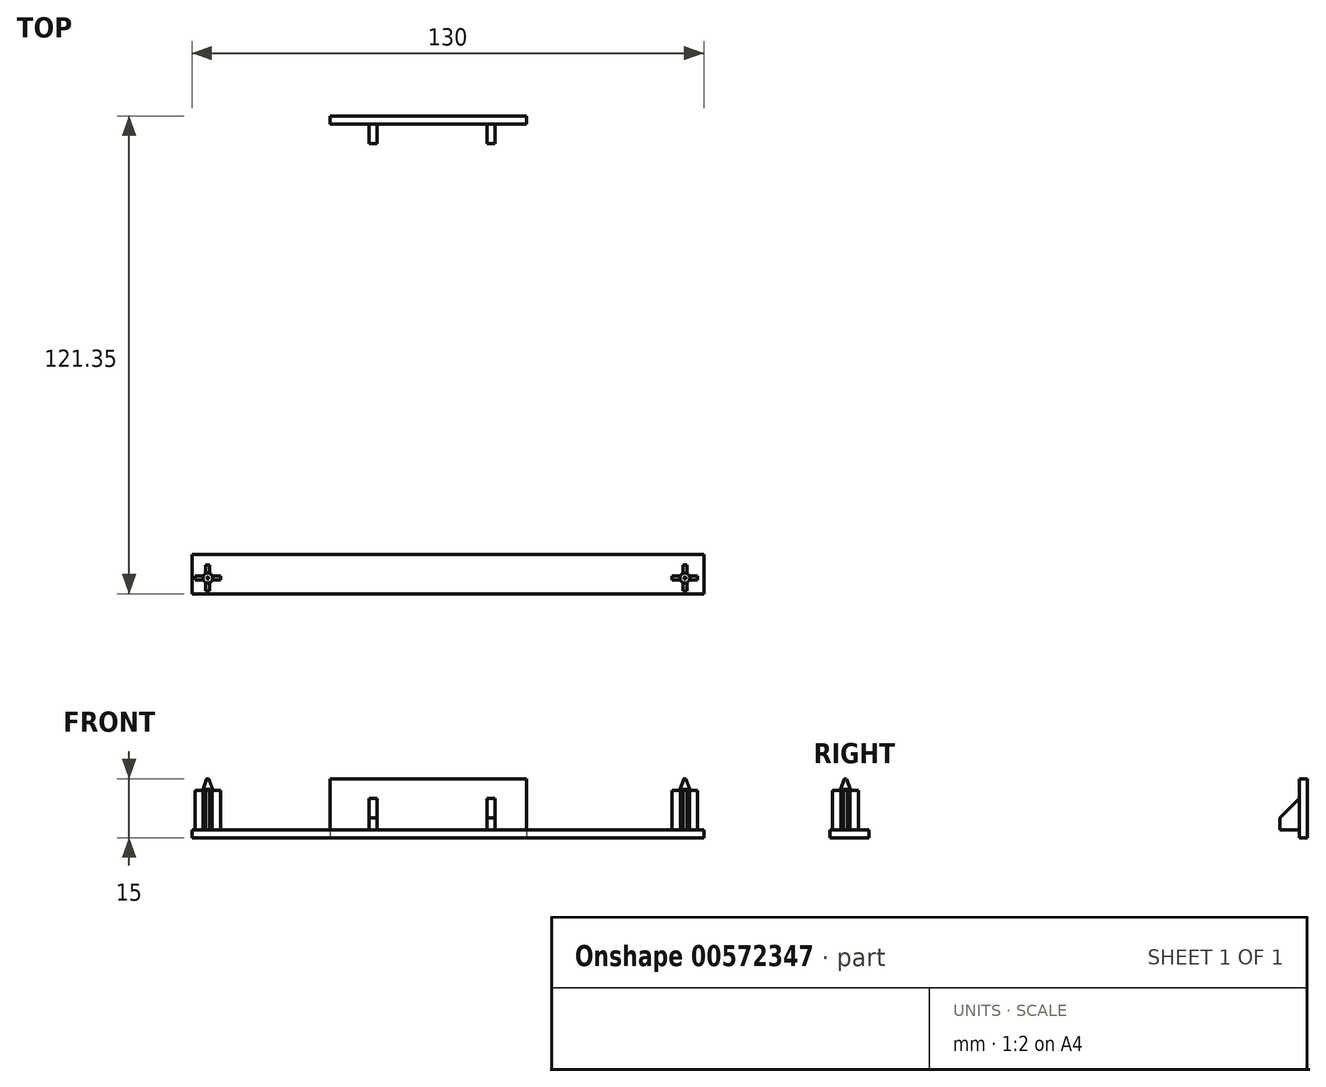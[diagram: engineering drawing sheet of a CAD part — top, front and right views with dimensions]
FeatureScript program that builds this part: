
annotation { "Feature Type Name" : "Feature", "Feature Type Description" : "" }
export const myFeature = defineFeature(function(context is Context, id is Id, definition is map)
    precondition{}
    {
        {
            var Q0;
            Q0=qCreatedBy(makeId("Top.planeOp"),FACE);
            var sketch = newSketch(context, id + "F0", { "sketchPlane" : qUnion([Q0])});
            skLineSegment(sketch, "E0.bottom", {"start": v(-65, 5) * mm, "end": v(65, 5) * mm});
            skLineSegment(sketch, "E0.top", {"start": v(-65, -5) * mm, "end": v(65, -5) * mm});
            skLineSegment(sketch, "E0.left", {"start": v(-65, 5) * mm, "end": v(-65, -5) * mm});
            skLineSegment(sketch, "E0.right", {"start": v(65, 5) * mm, "end": v(65, -5) * mm});
            skPoint(sketch, "E0.middle", {"position": v(0, 0) * mm});
            skCircle(sketch, "E1", {"center": v(-61, -1) * mm, "radius": 1.25 * mm});
            skCircle(sketch, "E2", {"center": v(60.2, -1) * mm, "radius": 1.25 * mm});
            skLineSegment(sketch, "E3.bottom", {"start": v(20, 116.35) * mm, "end": v(-30, 116.35) * mm});
            skLineSegment(sketch, "E3.top", {"start": v(20, 114.35) * mm, "end": v(-30, 114.35) * mm});
            skLineSegment(sketch, "E3.left", {"start": v(20, 116.35) * mm, "end": v(20, 114.35) * mm});
            skLineSegment(sketch, "E3.right", {"start": v(-30, 116.35) * mm, "end": v(-30, 114.35) * mm});
            skLineSegment(sketch, "E4.bottom", {"start": v(-30, 114.35) * mm, "end": v(20, 114.35) * mm});
            skLineSegment(sketch, "E4.top", {"start": v(-30, 5) * mm, "end": v(20, 5) * mm});
            skLineSegment(sketch, "E4.left", {"start": v(-30, 114.35) * mm, "end": v(-30, 5) * mm});
            skLineSegment(sketch, "E4.right", {"start": v(20, 114.35) * mm, "end": v(20, 5) * mm});
            skLineSegment(sketch, "E5.bottom", {"start": v(10, 5) * mm, "end": v(-20, 5) * mm});
            skLineSegment(sketch, "E5.top", {"start": v(10, 104.35) * mm, "end": v(-20, 104.35) * mm});
            skLineSegment(sketch, "E5.left", {"start": v(10, 5) * mm, "end": v(10, 104.35) * mm});
            skLineSegment(sketch, "E5.right", {"start": v(-20, 5) * mm, "end": v(-20, 104.35) * mm});
            skSolve(sketch);
        }
        {
            var Q0;
            Q0=makeQuery(id+"F0.imprint","IMPRINT",FACE,{"disambiguationData":[TD([[makeQuery(id+"F0.imprint","IMPRINT",EDGE,{"derivedFrom":sQuery(id+"F0.wireOp",EDGE,"E0.bottom")}),-1.0]])]});
            var Q1;
            Q1=makeQuery(id+"F0.imprint","IMPRINT",FACE,{"disambiguationData":[TD([[makeQuery(id+"F0.imprint","IMPRINT",EDGE,{"derivedFrom":sQuery(id+"F0.wireOp",EDGE,"XagRdlXz-Ve0I-5g32-Q18D-jBkH4EqLrLiy.top")}),1.0]])]});
            var Q2;
            Q2=makeQuery(id+"F0.imprint","IMPRINT",FACE,{"disambiguationData":[TD([[makeQuery(id+"F0.imprint","IMPRINT",EDGE,{"derivedFrom":sQuery(id+"F0.wireOp",EDGE,"E1")}),1.0]])]});
            var Q3;
            Q3=makeQuery(id+"F0.imprint","IMPRINT",FACE,{"disambiguationData":[TD([[makeQuery(id+"F0.imprint","IMPRINT",EDGE,{"derivedFrom":sQuery(id+"F0.wireOp",EDGE,"E2")}),1.0]])]});
            var Q4;
            Q4=makeQuery(id+"F0.imprint","IMPRINT",FACE,{"disambiguationData":[TD([[makeQuery(id+"F0.imprint","IMPRINT",EDGE,{"derivedFrom":sQuery(id+"F0.wireOp",EDGE,"5H1ODwpn-zWHE-gUJH-5W54-b54j58Tz3pfE.bottom")}),-1.0]])]});
            var Q5;
            Q5=makeQuery(id+"F0.imprint","IMPRINT",FACE,{"disambiguationData":[TD([[makeQuery(id+"F0.imprint","IMPRINT",EDGE,{"derivedFrom":sQuery(id+"F0.wireOp",EDGE,"2Jnmmmqf-Rcg9-hCOh-pptU-cnoVZbbS0fhq")}),1.0]])]});
            var Q6;
            Q6=makeQuery(id+"F0.imprint","IMPRINT",FACE,{"disambiguationData":[TD([[makeQuery(id+"F0.imprint","IMPRINT",EDGE,{"derivedFrom":sQuery(id+"F0.wireOp",EDGE,"tbl0VOvq-DBB5-Cd5s-9SjX-9i5cYzIEWrNP")}),1.0]])]});
            var Q7;
            Q7=makeQuery(id+"F0.imprint","IMPRINT",FACE,{"disambiguationData":[TD([[makeQuery(id+"F0.imprint","IMPRINT",EDGE,{"derivedFrom":sQuery(id+"F0.wireOp",EDGE,"E4.bottom")}),-1.0]])]});
            extrude(context, id + "F1", {"entities" : qUnion([Q0, Q1, Q2, Q3, Q4, Q5, Q6, Q7]), "depth" : 2 * mm, "offsetDistance" : 25 * mm});
        }
        {
            var Q0;
            Q0=makeQuery(id+"F0.imprint","IMPRINT",FACE,{"disambiguationData":[TD([[makeQuery(id+"F0.imprint","IMPRINT",EDGE,{"derivedFrom":sQuery(id+"F0.wireOp",EDGE,"WWVvqCjI-q0WO-kq73-eubj-YrUGcLexn1K2.top")}),-1.0]])]});
            var Q1;
            Q1=makeQuery(id+"F0.imprint","IMPRINT",FACE,{"disambiguationData":[TD([[makeQuery(id+"F0.imprint","IMPRINT",EDGE,{"derivedFrom":sQuery(id+"F0.wireOp",EDGE,"5H1ODwpn-zWHE-gUJH-5W54-b54j58Tz3pfE.bottom")}),-1.0]])]});
            var Q2;
            Q2=makeQuery(id+"F0.imprint","IMPRINT",FACE,{"disambiguationData":[TD([[makeQuery(id+"F0.imprint","IMPRINT",EDGE,{"derivedFrom":sQuery(id+"F0.wireOp",EDGE,"E2")}),1.0]])]});
            var Q3;
            Q3=makeQuery(id+"F0.imprint","IMPRINT",FACE,{"disambiguationData":[TD([[makeQuery(id+"F0.imprint","IMPRINT",EDGE,{"derivedFrom":sQuery(id+"F0.wireOp",EDGE,"E1")}),1.0]])]});
            var Q4;
            Q4=makeQuery(id+"F0.imprint","IMPRINT",FACE,{"disambiguationData":[TD([[makeQuery(id+"F0.imprint","IMPRINT",EDGE,{"derivedFrom":sQuery(id+"F0.wireOp",EDGE,"tbl0VOvq-DBB5-Cd5s-9SjX-9i5cYzIEWrNP")}),1.0]])]});
            var Q5;
            Q5=makeQuery(id+"F0.imprint","IMPRINT",FACE,{"disambiguationData":[TD([[makeQuery(id+"F0.imprint","IMPRINT",EDGE,{"derivedFrom":sQuery(id+"F0.wireOp",EDGE,"2Jnmmmqf-Rcg9-hCOh-pptU-cnoVZbbS0fhq")}),1.0]])]});
            var Q6;
            Q6=makeQuery(id+"F0.imprint","IMPRINT",FACE,{"disambiguationData":[TD([[makeQuery(id+"F0.imprint","IMPRINT",EDGE,{"derivedFrom":sQuery(id+"F0.wireOp",EDGE,"E3.bottom")}),1.0]])]});
            extrude(context, id + "F2", {"entities" : qUnion([Q0, Q1, Q2, Q3, Q4, Q5, Q6]), "operationType" : NewBodyOperationType.ADD, "depth" : 15 * mm, "offsetDistance" : 25 * mm});
        }
        {
            var Q0;
            Q0=makeQuery(id+"F2.opExtrude","CAP_EDGE",EDGE,{"disambiguationData":[OSD([sQuery(id+"F0.wireOp",EDGE,"E2")])],"isStart":false});
            var Q1;
            Q1=makeQuery(id+"F2.opExtrude","CAP_EDGE",EDGE,{"disambiguationData":[OSD([sQuery(id+"F0.wireOp",EDGE,"E1")])],"isStart":false});
            var Q2;
            Q2=makeQuery(id+"F2.opExtrude","CAP_EDGE",EDGE,{"disambiguationData":[OSD([sQuery(id+"F0.wireOp",EDGE,"E4.bottom")])],"isStart":false});
            chamfer(context, id + "F3", {"entities" : qUnion([Q0, Q1, Q2]), "chamferType" : ChamferType.OFFSET_ANGLE, "width" : 1 * mm, "oppositeDirection" : false, "angle" : 70 * degree, "tangentPropagation" : true});
        }
        {
            var Q0;
            Q0=makeQuery(id+"F1.opExtrude","CAP_FACE",FACE,{"disambiguationData":[OSD([sQuery(id+"F0.wireOp",EDGE,"E0.bottom"),sQuery(id+"F0.wireOp",EDGE,"E0.top"),sQuery(id+"F0.wireOp",EDGE,"E0.left"),sQuery(id+"F0.wireOp",EDGE,"E0.right"),sQuery(id+"F0.wireOp",EDGE,"E4.bottom"),sQuery(id+"F0.wireOp",EDGE,"E4.left"),sQuery(id+"F0.wireOp",EDGE,"E4.right"),sQuery(id+"F0.wireOp",EDGE,"E5.bottom"),sQuery(id+"F0.wireOp",EDGE,"E5.top"),sQuery(id+"F0.wireOp",EDGE,"E5.left"),sQuery(id+"F0.wireOp",EDGE,"E5.right")])],"isStart":false});
            var sketch = newSketch(context, id + "F4", { "sketchPlane" : qUnion([Q0])});
            skLineSegment(sketch, "E6.bottom", {"start": v(-64.25, -0.5) * mm, "end": v(-57.75, -0.5) * mm});
            skLineSegment(sketch, "E6.top", {"start": v(-64.25, -1.5) * mm, "end": v(-57.75, -1.5) * mm});
            skLineSegment(sketch, "E6.left", {"start": v(-64.25, -0.5) * mm, "end": v(-64.25, -1.5) * mm});
            skLineSegment(sketch, "E6.right", {"start": v(-57.75, -0.5) * mm, "end": v(-57.75, -1.5) * mm});
            skLineSegment(sketch, "E7.bottom", {"start": v(-61.5, 2.25) * mm, "end": v(-60.5, 2.25) * mm});
            skLineSegment(sketch, "E7.top", {"start": v(-61.5, -4.25) * mm, "end": v(-60.5, -4.25) * mm});
            skLineSegment(sketch, "E7.left", {"start": v(-61.5, 2.25) * mm, "end": v(-61.5, -4.25) * mm});
            skLineSegment(sketch, "E7.right", {"start": v(-60.5, 2.25) * mm, "end": v(-60.5, -4.25) * mm});
            skLineSegment(sketch, "E8.bottom", {"start": v(59.7, 2.25) * mm, "end": v(60.7, 2.25) * mm});
            skLineSegment(sketch, "E8.top", {"start": v(59.7, -4.25) * mm, "end": v(60.7, -4.25) * mm});
            skLineSegment(sketch, "E8.left", {"start": v(59.7, 2.25) * mm, "end": v(59.7, -4.25) * mm});
            skLineSegment(sketch, "E8.right", {"start": v(60.7, 2.25) * mm, "end": v(60.7, -4.25) * mm});
            skLineSegment(sketch, "E9.bottom", {"start": v(56.95, -0.5) * mm, "end": v(63.45, -0.5) * mm});
            skLineSegment(sketch, "E9.top", {"start": v(56.95, -1.5) * mm, "end": v(63.45, -1.5) * mm});
            skLineSegment(sketch, "E9.left", {"start": v(56.95, -0.5) * mm, "end": v(56.95, -1.5) * mm});
            skLineSegment(sketch, "E9.right", {"start": v(63.45, -0.5) * mm, "end": v(63.45, -1.5) * mm});
            skSolve(sketch);
        }
        {
            var Q0;
            Q0 = qSketchRegion(id + "F4", true);
            extrude(context, id + "F5", {"entities" : qUnion([Q0]), "operationType" : NewBodyOperationType.ADD, "depth" : 10 * mm, "offsetDistance" : 25 * mm});
        }
        {
            var Q0;
            Q0=makeQuery(id+"F1.opExtrude","CAP_FACE",FACE,{"disambiguationData":[OSD([sQuery(id+"F0.wireOp",EDGE,"E0.bottom"),sQuery(id+"F0.wireOp",EDGE,"E0.top"),sQuery(id+"F0.wireOp",EDGE,"E0.left"),sQuery(id+"F0.wireOp",EDGE,"E0.right"),sQuery(id+"F0.wireOp",EDGE,"E4.bottom"),sQuery(id+"F0.wireOp",EDGE,"E4.left"),sQuery(id+"F0.wireOp",EDGE,"E4.right"),sQuery(id+"F0.wireOp",EDGE,"E5.bottom"),sQuery(id+"F0.wireOp",EDGE,"E5.top"),sQuery(id+"F0.wireOp",EDGE,"E5.left"),sQuery(id+"F0.wireOp",EDGE,"E5.right")])],"isStart":false});
            var sketch = newSketch(context, id + "F6", { "sketchPlane" : qUnion([Q0])});
            skLineSegment(sketch, "E10.bottom", {"start": v(-20, 114.35) * mm, "end": v(-18, 114.35) * mm});
            skLineSegment(sketch, "E10.top", {"start": v(-20, 109.35) * mm, "end": v(-18, 109.35) * mm});
            skLineSegment(sketch, "E10.left", {"start": v(-20, 114.35) * mm, "end": v(-20, 109.35) * mm});
            skLineSegment(sketch, "E10.right", {"start": v(-18, 114.35) * mm, "end": v(-18, 109.35) * mm});
            skLineSegment(sketch, "E11.bottom", {"start": v(10, 114.35) * mm, "end": v(12, 114.35) * mm});
            skLineSegment(sketch, "E11.top", {"start": v(10, 109.35) * mm, "end": v(12, 109.35) * mm});
            skLineSegment(sketch, "E11.left", {"start": v(10, 114.35) * mm, "end": v(10, 109.35) * mm});
            skLineSegment(sketch, "E11.right", {"start": v(12, 114.35) * mm, "end": v(12, 109.35) * mm});
            skSolve(sketch);
        }
        {
            var Q0;
            Q0 = qSketchRegion(id + "F6", true);
            extrude(context, id + "F7", {"entities" : qUnion([Q0]), "operationType" : NewBodyOperationType.ADD, "depth" : 8 * mm, "offsetDistance" : 25 * mm});
        }
        {
            var Q0;
            Q0=makeQuery(id+"F7.opExtrude","CAP_EDGE",EDGE,{"disambiguationData":[OSD([sQuery(id+"F6.wireOp",EDGE,"E10.top")])],"isStart":false});
            var Q1;
            Q1=makeQuery(id+"F7.opExtrude","CAP_EDGE",EDGE,{"disambiguationData":[OSD([sQuery(id+"F6.wireOp",EDGE,"E11.top")])],"isStart":false});
            chamfer(context, id + "F8", {"entities" : qUnion([Q0, Q1]), "width" : 5 * mm, "tangentPropagation" : true});
        }
    });
